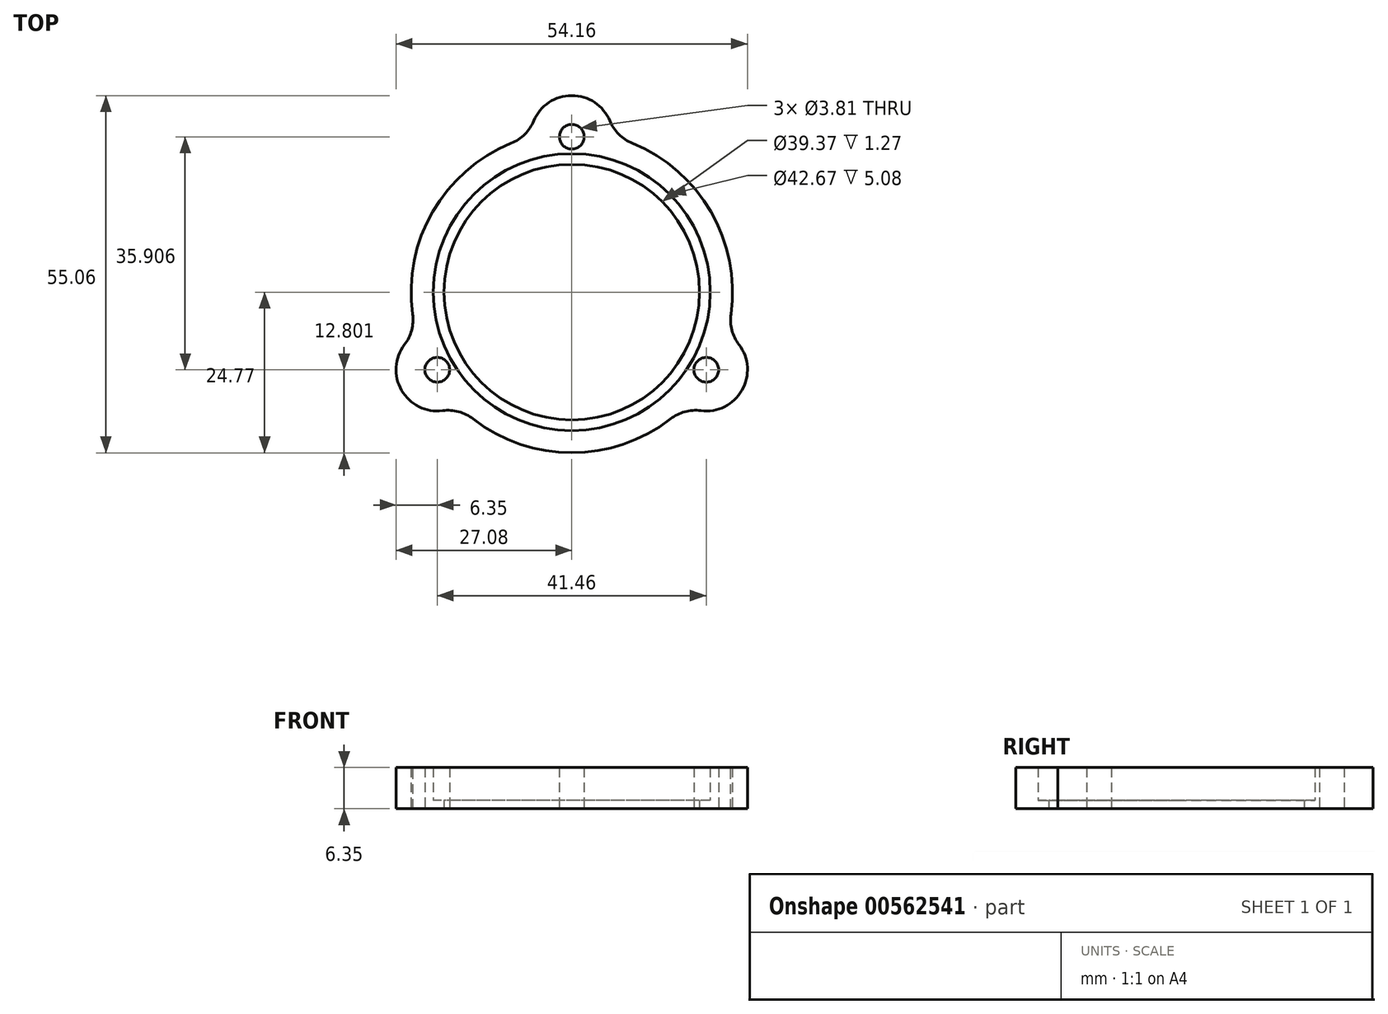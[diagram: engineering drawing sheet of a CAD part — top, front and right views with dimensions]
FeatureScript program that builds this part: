
annotation { "Feature Type Name" : "Feature", "Feature Type Description" : "" }
export const myFeature = defineFeature(function(context is Context, id is Id, definition is map)
    precondition{}
    {
        {
            var Q0;
            Q0=qCreatedBy(makeId("Top.planeOp"),FACE);
            var sketch = newSketch(context, id + "F0", { "sketchPlane" : qUnion([Q0])});
            skCircle(sketch, "E0", {"center": v(0, 0) * mm, "radius": 21.34 * mm});
            skCircle(sketch, "E1", {"center": v(0, 0) * mm, "radius": 19.69 * mm});
            skCircle(sketch, "E2", {"center": v(0, 0) * mm, "radius": 24.77 * mm});
            skLineSegment(sketch, "E3", {"start": v(0, 0) * mm, "end": v(0, 42.77) * mm, "construction": true});
            skLineSegment(sketch, "E4", {"start": v(0, 0) * mm, "end": v(-43.71, -25.24) * mm, "construction": true});
            skLineSegment(sketch, "E5", {"start": v(0, 0) * mm, "end": v(46.9, -27.08) * mm, "construction": true});
            skLineSegment(sketch, "E6", {"start": v(-6.35, 2.16) * mm, "end": v(-6.35, 48.97) * mm, "construction": true});
            skLineSegment(sketch, "E7.MirrorCS", {"start": v(6.35, 2.16) * mm, "end": v(6.35, 48.97) * mm, "construction": true});
            skLineSegment(sketch, "E8", {"start": v(-11.23, 0.85) * mm, "end": v(-48.99, -20.95) * mm, "construction": true});
            skLineSegment(sketch, "E9.MirrorCS", {"start": v(-4.88, -10.15) * mm, "end": v(-42.64, -31.95) * mm, "construction": true});
            skLineSegment(sketch, "E10", {"start": v(0.14, -7.41) * mm, "end": v(38.48, -29.55) * mm, "construction": true});
            skLineSegment(sketch, "E11.MirrorCS", {"start": v(6.49, 3.59) * mm, "end": v(44.83, -18.55) * mm, "construction": true});
            skArc(sketch, "E12", {"start": v(6.35, 23.94) * mm, "mid": v(0, 30.29) * mm, "end": v(-6.35, 23.94) * mm});
            skArc(sketch, "E13", {"start": v(-23.9, -6.47) * mm, "mid": v(-26.23, -15.14) * mm, "end": v(-17.56, -17.47) * mm});
            skArc(sketch, "E14", {"start": v(17.56, -17.47) * mm, "mid": v(26.23, -15.14) * mm, "end": v(23.9, -6.47) * mm});
            skCircle(sketch, "E15", {"center": v(0, 23.94) * mm, "radius": 1.9 * mm});
            skCircle(sketch, "E16", {"center": v(-20.73, -11.97) * mm, "radius": 1.9 * mm});
            skCircle(sketch, "E17", {"center": v(20.73, -11.97) * mm, "radius": 1.9 * mm});
            skSolve(sketch);
        }
        {
            var Q0;
            Q0=makeQuery(id+"F0.imprint","IMPRINT",FACE,{"disambiguationData":[TD([[makeQuery(id+"F0.imprint","IMPRINT",EDGE,{"derivedFrom":sQuery(id+"F0.wireOp",EDGE,"E0")}),1.0]])]});
            extrude(context, id + "F1", {"entities" : qUnion([Q0]), "depth" : 1.27 * mm, "offsetDistance" : 25.4 * mm});
        }
        {
            var Q0;
            Q0=qSketchRegion(id+"F0",true);
            extrude(context, id + "F2", {"entities" : qUnion([Q0]), "operationType" : NewBodyOperationType.ADD, "depth" : 6.35 * mm, "offsetDistance" : 25.4 * mm});
        }
        {
            var Q0;
            {var subQ0=sQuery(id+"F0.wireOp",EDGE,"E12");var subQ1=sQuery(id+"F0.wireOp",EDGE,"E2");Q0=makeQuery(id+"F2.opExtrude","SWEPT_EDGE",EDGE,{"disambiguationData":[OSD([subQ1,subQ0]),TDD([makeQuery(id+"F0.imprint","INTERSECT",VERTEX,{"disambiguationData":[OD(0.0)],"derivedFrom":[subQ1,subQ0]})])]});}
            var Q1;
            {var subQ0=sQuery(id+"F0.wireOp",EDGE,"E12");var subQ1=sQuery(id+"F0.wireOp",EDGE,"E2");Q1=makeQuery(id+"F2.opExtrude","SWEPT_EDGE",EDGE,{"disambiguationData":[OSD([subQ1,subQ0]),TDD([makeQuery(id+"F0.imprint","INTERSECT",VERTEX,{"disambiguationData":[OD(1.0)],"derivedFrom":[subQ1,subQ0]})])]});}
            var Q2;
            {var subQ0=sQuery(id+"F0.wireOp",EDGE,"E13");var subQ1=sQuery(id+"F0.wireOp",EDGE,"E2");Q2=makeQuery(id+"F2.opExtrude","SWEPT_EDGE",EDGE,{"disambiguationData":[OSD([subQ1,subQ0]),TDD([makeQuery(id+"F0.imprint","INTERSECT",VERTEX,{"disambiguationData":[OD(0.0)],"derivedFrom":[subQ1,subQ0]})])]});}
            var Q3;
            {var subQ0=sQuery(id+"F0.wireOp",EDGE,"E13");var subQ1=sQuery(id+"F0.wireOp",EDGE,"E2");Q3=makeQuery(id+"F2.opExtrude","SWEPT_EDGE",EDGE,{"disambiguationData":[OSD([subQ1,subQ0]),TDD([makeQuery(id+"F0.imprint","INTERSECT",VERTEX,{"disambiguationData":[OD(1.0)],"derivedFrom":[subQ1,subQ0]})])]});}
            var Q4;
            {var subQ0=sQuery(id+"F0.wireOp",EDGE,"E14");var subQ1=sQuery(id+"F0.wireOp",EDGE,"E2");Q4=makeQuery(id+"F2.opExtrude","SWEPT_EDGE",EDGE,{"disambiguationData":[OSD([subQ1,subQ0]),TDD([makeQuery(id+"F0.imprint","INTERSECT",VERTEX,{"disambiguationData":[OD(1.0)],"derivedFrom":[subQ1,subQ0]})])]});}
            var Q5;
            {var subQ0=sQuery(id+"F0.wireOp",EDGE,"E14");var subQ1=sQuery(id+"F0.wireOp",EDGE,"E2");Q5=makeQuery(id+"F2.opExtrude","SWEPT_EDGE",EDGE,{"disambiguationData":[OSD([subQ1,subQ0]),TDD([makeQuery(id+"F0.imprint","INTERSECT",VERTEX,{"disambiguationData":[OD(0.0)],"derivedFrom":[subQ1,subQ0]})])]});}
            fillet(context, id + "F3", {"entities" : qUnion([Q0, Q1, Q2, Q3, Q4, Q5]), "radius" : 6.35 * mm, "tangentPropagation" : true, "allowEdgeOverflow" : false});
        }
    });
